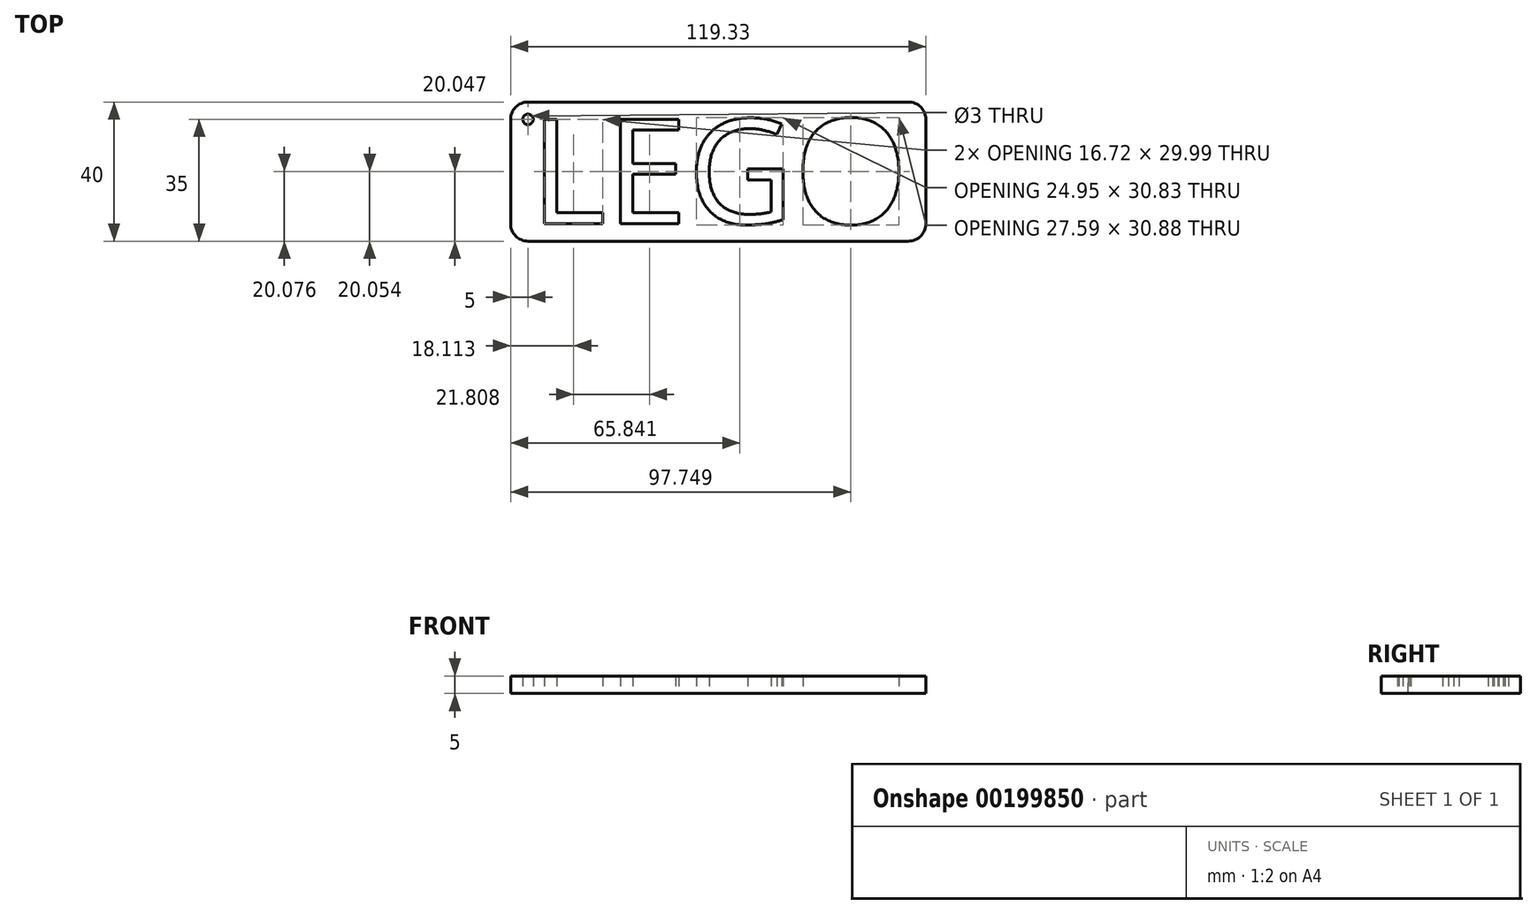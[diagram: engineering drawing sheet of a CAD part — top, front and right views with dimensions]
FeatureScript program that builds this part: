
annotation { "Feature Type Name" : "Feature", "Feature Type Description" : "" }
export const myFeature = defineFeature(function(context is Context, id is Id, definition is map)
    precondition{}
    {
        {
            var Q0;
            Q0=qCreatedBy(makeId("Top.planeOp"),FACE);
            var sketch = newSketch(context, id + "F0", { "sketchPlane" : qUnion([Q0])});
            skLineSegment(sketch, "E0.bottom", {"start": v(5, 0) * mm, "end": v(114.28, 0) * mm});
            skLineSegment(sketch, "E0.top", {"start": v(5.05, 40) * mm, "end": v(114.28, 40) * mm});
            skLineSegment(sketch, "E0.left", {"start": v(0, 5) * mm, "end": v(0, 34.95) * mm});
            skLineSegment(sketch, "E0.right", {"start": v(119.33, 5.05) * mm, "end": v(119.33, 34.95) * mm});
            skPoint(sketch, "E1.visualSharp", {"position": v(0, 40) * mm});
            skArc(sketch, "E1.filletArc", {"start": v(5.05, 40) * mm, "mid": v(1.48, 38.52) * mm, "end": v(0, 34.95) * mm});
            skPoint(sketch, "E2.visualSharp", {"position": v(0, 0) * mm});
            skArc(sketch, "E2.filletArc", {"start": v(0, 5) * mm, "mid": v(1.46, 1.46) * mm, "end": v(5, 0) * mm});
            skPoint(sketch, "E3.visualSharp", {"position": v(119.33, 0) * mm});
            skArc(sketch, "E3.filletArc", {"start": v(114.28, 0) * mm, "mid": v(117.85, 1.48) * mm, "end": v(119.33, 5.05) * mm});
            skPoint(sketch, "E4.visualSharp", {"position": v(119.33, 40) * mm});
            skArc(sketch, "E4.filletArc", {"start": v(119.33, 34.95) * mm, "mid": v(117.85, 38.52) * mm, "end": v(114.28, 40) * mm});
            skCircle(sketch, "E5", {"center": v(5, 35) * mm, "radius": 1.5 * mm});
            skText(sketch, "E6", { "text": "LEGO", "fontName": "OpenSans-Regular.ttf"});
            const initialGuessF0  = {"E6": [0.00563, 0.00505, 1, 0, 0.03025]};
            skSetInitialGuess(sketch, initialGuessF0);
            skSolve(sketch);
        }
        {
            var Q0;
            Q0 = qSketchRegion(id + "F0", true);
            extrude(context, id + "F1", {"entities" : qUnion([Q0]), "depth" : 5 * mm});
        }
    });
